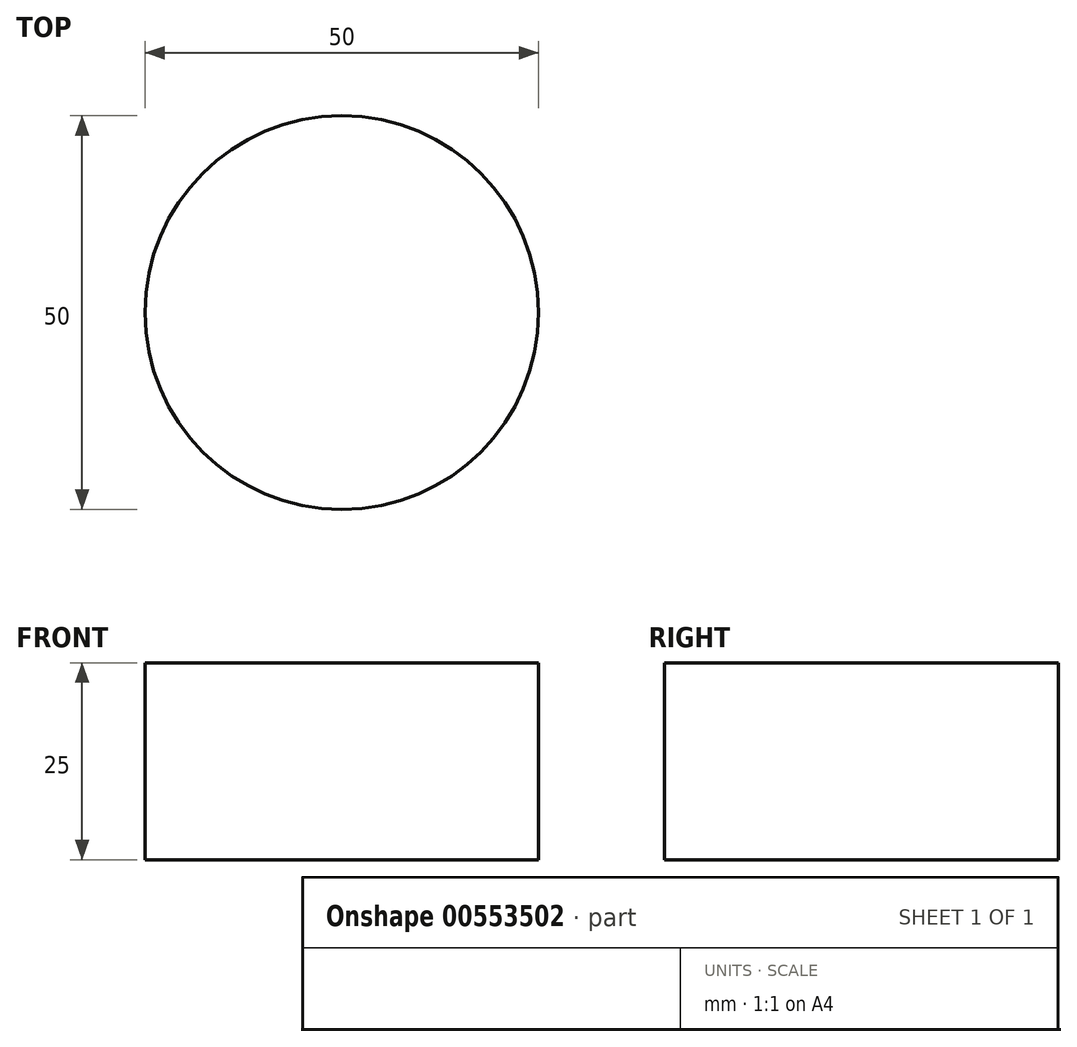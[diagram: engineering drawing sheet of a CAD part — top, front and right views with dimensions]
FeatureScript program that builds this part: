
annotation { "Feature Type Name" : "Feature", "Feature Type Description" : "" }
export const myFeature = defineFeature(function(context is Context, id is Id, definition is map)
    precondition{}
    {
        {
            var Q0;
            Q0=qCreatedBy(makeId("Top.planeOp"),FACE);
            var sketch = newSketch(context, id + "F0", { "sketchPlane" : qUnion([Q0])});
            skCircle(sketch, "E0", {"center": v(0, 0) * mm, "radius": 25 * mm});
            skCircle(sketch, "E1", {"center": v(0, 0) * mm, "radius": 5 * mm});
            skSolve(sketch);
        }
        {
            var Q0;
            Q0 = qSketchRegion(id + "F0", true);
            extrude(context, id + "F1", {"entities" : qUnion([Q0]), "depth" : 25 * mm, "offsetDistance" : 25 * mm});
        }
        {
            var Q0;
            Q0=makeQuery(id+"F0.imprint","IMPRINT",FACE,{"disambiguationData":[TD([[makeQuery(id+"F0.imprint","IMPRINT",EDGE,{"derivedFrom":sQuery(id+"F0.wireOp",EDGE,"E1")}),1.0]])]});
            extrude(context, id + "F2", {"entities" : qUnion([Q0]), "operationType" : NewBodyOperationType.ADD, "depth" : 25 * mm, "offsetDistance" : 25 * mm});
        }
    });
